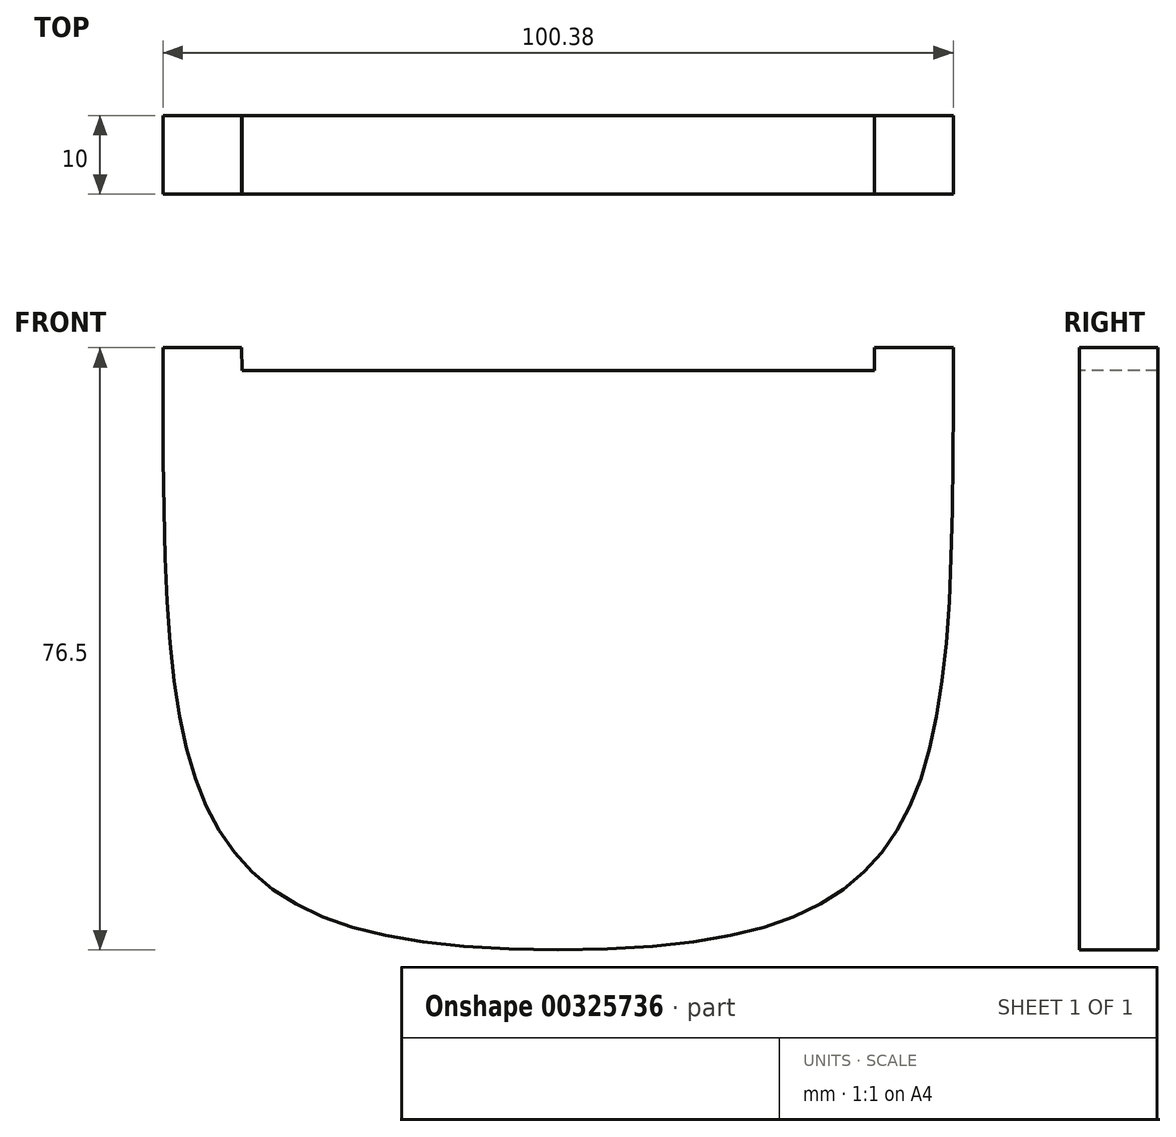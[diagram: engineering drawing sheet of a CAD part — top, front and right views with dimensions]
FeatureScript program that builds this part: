
annotation { "Feature Type Name" : "Feature", "Feature Type Description" : "" }
export const myFeature = defineFeature(function(context is Context, id is Id, definition is map)
    precondition{}
    {
        {
            var Q0;
            Q0=qCreatedBy(makeId("Front.planeOp"),FACE);
            var sketch = newSketch(context, id + "F0", { "sketchPlane" : qUnion([Q0])});
            skLineSegment(sketch, "E0", {"start": v(-49.81, 0) * mm, "end": v(50.19, 0) * mm, "construction": true});
            skLineSegment(sketch, "E1", {"start": v(50.19, 0) * mm, "end": v(50.19, 76.5) * mm, "construction": true});
            skLineSegment(sketch, "E2", {"start": v(0, 0) * mm, "end": v(0, 95.66) * mm});
            skFitSpline(sketch, "E3", {"points": [v(0, 0) * mm, v(50.19, 76.5) * mm], "startDerivative": vector(150.56, 0) * mm, "endDerivative": vector(0, 172.54) * mm});
            skFitSpline(sketch, "E4.MirrorCS", {"points": [v(0, 0) * mm, v(-50.19, 76.5) * mm], "startDerivative": vector(-150.56, 0) * mm, "endDerivative": vector(0, 172.54) * mm});
            skFitSpline(sketch, "E5.0", {"points": [v(0, 10) * mm, v(-2.98, 10) * mm, v(-8.5, 10.14) * mm, v(-15.47, 10.78) * mm, v(-21.18, 11.8) * mm, v(-25.65, 13.18) * mm, v(-29, 14.78) * mm, v(-31.47, 16.55) * mm, v(-33.41, 18.6) * mm, v(-35.1, 21.2) * mm, v(-36.58, 24.63) * mm, v(-37.83, 29.05) * mm, v(-38.8, 34.48) * mm, v(-39.48, 40.91) * mm, v(-39.9, 48.33) * mm, v(-40.18, 59.5) * mm, v(-40.19, 69.31) * mm, v(-40.19, 76.5) * mm]});
            skFitSpline(sketch, "E6.0", {"points": [v(0, 10) * mm, v(2.98, 10) * mm, v(8.5, 10.14) * mm, v(15.47, 10.78) * mm, v(21.18, 11.8) * mm, v(25.65, 13.18) * mm, v(29, 14.78) * mm, v(31.47, 16.55) * mm, v(33.41, 18.6) * mm, v(35.1, 21.2) * mm, v(36.58, 24.63) * mm, v(37.83, 29.05) * mm, v(38.8, 34.48) * mm, v(39.48, 40.91) * mm, v(39.9, 48.33) * mm, v(40.18, 59.5) * mm, v(40.19, 69.31) * mm, v(40.19, 76.5) * mm]});
            skLineSegment(sketch, "E7", {"start": v(-50.19, 76.5) * mm, "end": v(-40.19, 76.5) * mm});
            skLineSegment(sketch, "E8", {"start": v(40.19, 76.5) * mm, "end": v(50.19, 76.5) * mm});
            skPoint(sketch, "E9", {"position": v(-40.19, 73.63) * mm});
            skPoint(sketch, "E10", {"position": v(-151.06, 95.36) * mm});
            skPoint(sketch, "E11", {"position": v(40.19, 73.63) * mm});
            skPoint(sketch, "E12", {"position": v(-128.03, -7.05) * mm});
            skLineSegment(sketch, "E13", {"start": v(-40.19, 73.63) * mm, "end": v(40.19, 73.63) * mm});
            skSolve(sketch);
        }
        {
            var Q0;
            Q0 = qSketchRegion(id + "F0", true);
            extrude(context, id + "F1", {"entities" : qUnion([Q0]), "endBound" : BoundingType.SYMMETRIC, "depth" : 10 * mm});
        }
    });
